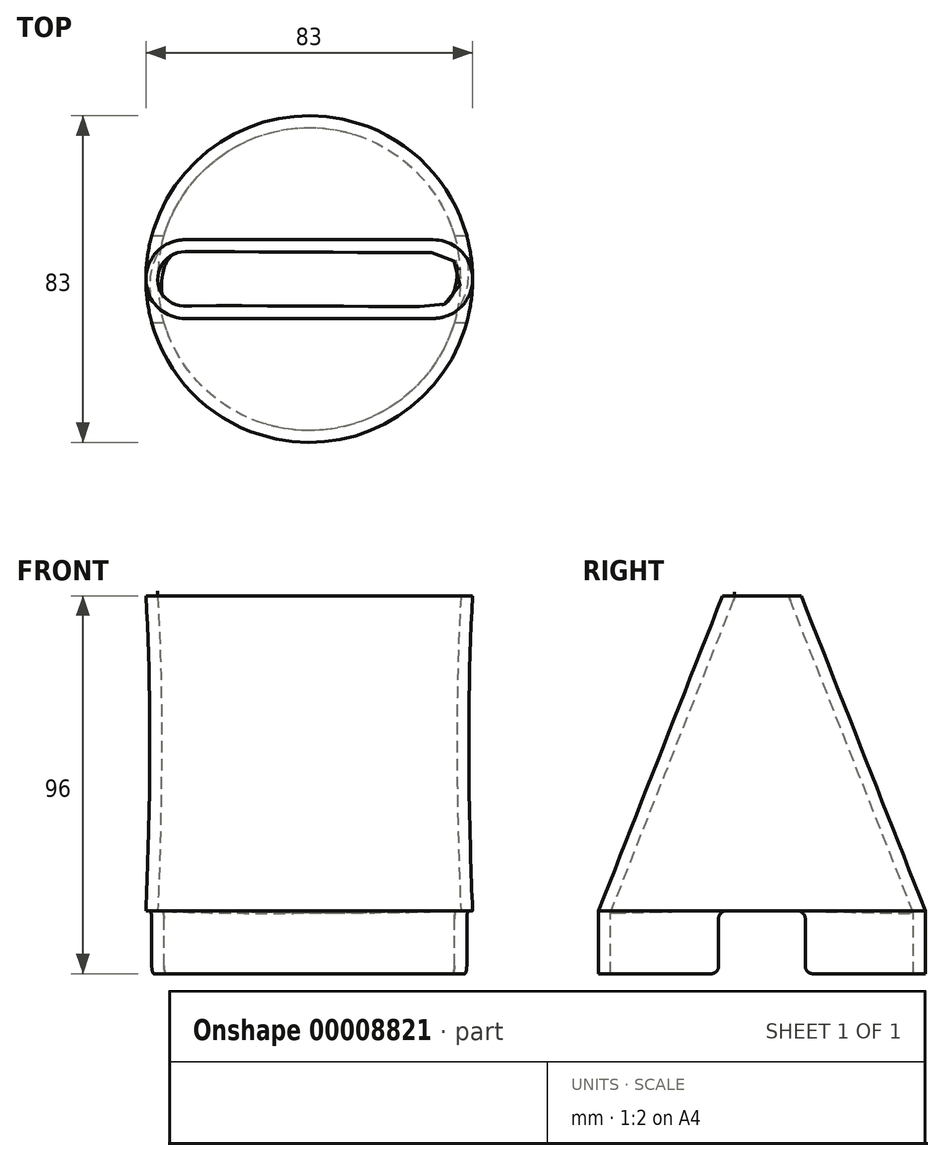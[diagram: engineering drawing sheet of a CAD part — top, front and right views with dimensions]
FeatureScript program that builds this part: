
annotation { "Feature Type Name" : "Feature", "Feature Type Description" : "" }
export const myFeature = defineFeature(function(context is Context, id is Id, definition is map)
    precondition{}
    {
        {
            var Q0;
            Q0=qCreatedBy(makeId("Top.planeOp"),FACE);
            var sketch = newSketch(context, id + "F0", { "sketchPlane" : qUnion([Q0])});
            skCircle(sketch, "E0", {"center": v(0, 0) * mm, "radius": 41.5 * mm});
            skSolve(sketch);
        }
        {
            var Q0;
            Q0=makeQuery(id+"F0.imprint","IMPRINT",FACE,{"disambiguationData":[TD([[makeQuery(id+"F0.imprint","IMPRINT",EDGE,{"derivedFrom":sQuery(id+"F0.wireOp",EDGE,"E0")}),1.0]])]});
            cPlane(context, id + "F1", {"entities" : qUnion([Q0]), "cplaneType" : CPlaneType.OFFSET, "offset" : 80 * mm, "width" : 150 * mm, "height" : 150 * mm});
        }
        {
            var Q0;
            Q0=qCreatedBy(id+"F1.planeOp",FACE);
            var sketch = newSketch(context, id + "F2", { "sketchPlane" : qUnion([Q0])});
            skLineSegment(sketch, "E1.bottom", {"start": v(-31.5, 10) * mm, "end": v(31.5, 10) * mm});
            skLineSegment(sketch, "E1.top", {"start": v(-31.5, -10) * mm, "end": v(31.5, -10) * mm});
            skLineSegment(sketch, "E1.left", {"start": v(-31.5, 10) * mm, "end": v(-31.5, -10) * mm, "construction": true});
            skLineSegment(sketch, "E1.right", {"start": v(31.5, 10) * mm, "end": v(31.5, -10) * mm, "construction": true});
            skPoint(sketch, "E2", {"position": v(0, -10) * mm});
            skPoint(sketch, "E3", {"position": v(31.5, 0) * mm});
            skArc(sketch, "E4", {"start": v(-31.5, 10) * mm, "mid": v(-41.5, 0) * mm, "end": v(-31.5, -10) * mm});
            skArc(sketch, "E5", {"start": v(31.5, -10) * mm, "mid": v(41.5, 0) * mm, "end": v(31.5, 10) * mm});
            skCircle(sketch, "E6.0", {"center": v(0, 0) * mm, "radius": 41.5 * mm});
            skPoint(sketch, "E7", {"position": v(41.5, 0) * mm});
            skSolve(sketch);
        }
        {
            var Q0;
            {var subQ3=sQuery(id+"F2.wireOp",EDGE,"E1.bottom");Q0=makeQuery(id+"F2.imprint","IMPRINT",FACE,{"disambiguationData":[TD([[makeQuery(id+"F2.imprint","IMPRINT",EDGE,{"derivedFrom":subQ3}),-1.0]])]});}
            var Q1;
            Q1=makeQuery(id+"F0.imprint","IMPRINT",FACE,{"disambiguationData":[TD([[makeQuery(id+"F0.imprint","IMPRINT",EDGE,{"derivedFrom":sQuery(id+"F0.wireOp",EDGE,"E0")}),1.0]])]});
            loft(context, id + "F3", {"sheetProfilesArray" : [{ "sheetProfileEntities" : qUnion([Q0]) }, { "sheetProfileEntities" : qUnion([Q1]) }]});
        }
        {
            var Q0;
            Q0=makeQuery(id+"F3.opLoft","CAP_FACE",FACE,{"disambiguationData":[OSD([makeQuery(id+"F0.imprint","IMPRINT",FACE,{"disambiguationData":[TD([[makeQuery(id+"F0.imprint","IMPRINT",EDGE,{"derivedFrom":sQuery(id+"F0.wireOp",EDGE,"E0")}),1.0]])]})])],"isStart":true});
            extrude(context, id + "F4", {"entities" : qUnion([Q0]), "operationType" : NewBodyOperationType.ADD, "depth" : 16 * mm});
        }
        {
            var Q0;
            {var subQ3=sQuery(id+"F2.wireOp",EDGE,"E1.bottom");Q0=makeQuery(id+"F3.opLoft","CAP_FACE",FACE,{"disambiguationData":[OSD([makeQuery(id+"F2.imprint","IMPRINT",FACE,{"disambiguationData":[TD([[makeQuery(id+"F2.imprint","IMPRINT",EDGE,{"derivedFrom":subQ3}),-1.0]])]})])],"isStart":true});}
            var Q1;
            Q1=makeQuery(id+"F4.opExtrude","CAP_FACE",FACE,{"disambiguationData":[OSD([makeQuery(id+"F0.imprint","IMPRINT",FACE,{"disambiguationData":[TD([[makeQuery(id+"F0.imprint","IMPRINT",EDGE,{"derivedFrom":sQuery(id+"F0.wireOp",EDGE,"E0")}),1.0]])]})])],"isStart":false});
            shell(context, id + "F5", {"entities" : qUnion([Q0, Q1]), "thickness" : 3 * mm});
        }
        {
            var Q0;
            Q0=qCreatedBy(makeId("Right.planeOp"),FACE);
            var sketch = newSketch(context, id + "F6", { "sketchPlane" : qUnion([Q0])});
            skLineSegment(sketch, "E8", {"start": v(0, 0) * mm, "end": v(11, 0) * mm});
            skLineSegment(sketch, "E9", {"start": v(11, 0) * mm, "end": v(11, -50) * mm});
            skLineSegment(sketch, "E10", {"start": v(11, -50) * mm, "end": v(-11, -50) * mm});
            skLineSegment(sketch, "E11", {"start": v(-11, -50) * mm, "end": v(-11, 0) * mm});
            skLineSegment(sketch, "E12", {"start": v(-11, 0) * mm, "end": v(0, 0) * mm});
            skPoint(sketch, "E13", {"position": v(0, -50) * mm});
            skSolve(sketch);
        }
        {
            var Q0;
            Q0=makeQuery(id+"F6.imprint","IMPRINT",FACE,{"disambiguationData":[TD([[makeQuery(id+"F6.imprint","IMPRINT",EDGE,{"derivedFrom":sQuery(id+"F6.wireOp",EDGE,"E8")}),-1.0]])]});
            extrude(context, id + "F7", {"entities" : qUnion([Q0]), "operationType" : NewBodyOperationType.REMOVE, "endBound" : BoundingType.THROUGH_ALL, "oppositeDirection" : true, "depth" : 25 * mm, "hasSecondDirection" : true, "secondDirectionBound" : SecondDirectionBoundingType.THROUGH_ALL, "secondDirectionOppositeDirection" : false, "secondDirectionDepth" : 25 * mm});
        }
        {
            var Q0;
            Q0=makeQuery(id+"F7.boolean.opBoolean","INTERSECT",EDGE,{"disambiguationData":[OD(1.0)],"derivedFrom":[makeQuery(id+"F4.opExtrude","CAP_FACE",FACE,{"disambiguationData":[OSD([makeQuery(id+"F0.imprint","IMPRINT",FACE,{"disambiguationData":[TD([[makeQuery(id+"F0.imprint","IMPRINT",EDGE,{"derivedFrom":sQuery(id+"F0.wireOp",EDGE,"E0")}),1.0]])]})])],"isStart":false}),makeQuery(id+"F7.opExtrude","SWEPT_FACE",FACE,{"disambiguationData":[OSD([sQuery(id+"F6.wireOp",EDGE,"E11")])]})]});
            var Q1;
            Q1=makeQuery(id+"F7.boolean.opBoolean","INTERSECT",EDGE,{"disambiguationData":[OD(1.0)],"derivedFrom":[makeQuery(id+"F4.opExtrude","CAP_FACE",FACE,{"disambiguationData":[OSD([makeQuery(id+"F0.imprint","IMPRINT",FACE,{"disambiguationData":[TD([[makeQuery(id+"F0.imprint","IMPRINT",EDGE,{"derivedFrom":sQuery(id+"F0.wireOp",EDGE,"E0")}),1.0]])]})])],"isStart":false}),makeQuery(id+"F7.opExtrude","SWEPT_FACE",FACE,{"disambiguationData":[OSD([sQuery(id+"F6.wireOp",EDGE,"E9")])]})]});
            var Q2;
            Q2=makeQuery(id+"F7.boolean.opBoolean","COPY",EDGE,{"disambiguationData":[OD(1.0)],"derivedFrom":makeQuery(id+"F7.opExtrude","SWEPT_EDGE",EDGE,{"disambiguationData":[OSD([sQuery(id+"F6.wireOp",EDGE,"E8"),sQuery(id+"F6.wireOp",EDGE,"E9")])]})});
            var Q3;
            Q3=makeQuery(id+"F7.boolean.opBoolean","COPY",EDGE,{"disambiguationData":[OD(1.0)],"derivedFrom":makeQuery(id+"F7.opExtrude","SWEPT_EDGE",EDGE,{"disambiguationData":[OSD([sQuery(id+"F6.wireOp",EDGE,"E11"),sQuery(id+"F6.wireOp",EDGE,"E12")])]})});
            var Q4;
            Q4=makeQuery(id+"F7.boolean.opBoolean","INTERSECT",EDGE,{"disambiguationData":[OD(0.0)],"derivedFrom":[makeQuery(id+"F4.opExtrude","CAP_FACE",FACE,{"disambiguationData":[OSD([makeQuery(id+"F0.imprint","IMPRINT",FACE,{"disambiguationData":[TD([[makeQuery(id+"F0.imprint","IMPRINT",EDGE,{"derivedFrom":sQuery(id+"F0.wireOp",EDGE,"E0")}),1.0]])]})])],"isStart":false}),makeQuery(id+"F7.opExtrude","SWEPT_FACE",FACE,{"disambiguationData":[OSD([sQuery(id+"F6.wireOp",EDGE,"E11")])]})]});
            var Q5;
            Q5=makeQuery(id+"F7.boolean.opBoolean","COPY",EDGE,{"disambiguationData":[OD(0.0)],"derivedFrom":makeQuery(id+"F7.opExtrude","SWEPT_EDGE",EDGE,{"disambiguationData":[OSD([sQuery(id+"F6.wireOp",EDGE,"E11"),sQuery(id+"F6.wireOp",EDGE,"E12")])]})});
            var Q6;
            Q6=makeQuery(id+"F7.boolean.opBoolean","COPY",EDGE,{"disambiguationData":[OD(0.0)],"derivedFrom":makeQuery(id+"F7.opExtrude","SWEPT_EDGE",EDGE,{"disambiguationData":[OSD([sQuery(id+"F6.wireOp",EDGE,"E8"),sQuery(id+"F6.wireOp",EDGE,"E9")])]})});
            var Q7;
            Q7=makeQuery(id+"F7.boolean.opBoolean","INTERSECT",EDGE,{"disambiguationData":[OD(0.0)],"derivedFrom":[makeQuery(id+"F4.opExtrude","CAP_FACE",FACE,{"disambiguationData":[OSD([makeQuery(id+"F0.imprint","IMPRINT",FACE,{"disambiguationData":[TD([[makeQuery(id+"F0.imprint","IMPRINT",EDGE,{"derivedFrom":sQuery(id+"F0.wireOp",EDGE,"E0")}),1.0]])]})])],"isStart":false}),makeQuery(id+"F7.opExtrude","SWEPT_FACE",FACE,{"disambiguationData":[OSD([sQuery(id+"F6.wireOp",EDGE,"E9")])]})]});
            fillet(context, id + "F8", {"entities" : qUnion([Q0, Q1, Q2, Q3, Q4, Q5, Q6, Q7]), "radius" : 2 * mm, "tangentPropagation" : true, "allowEdgeOverflow" : false});
        }
    });
